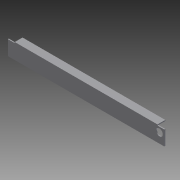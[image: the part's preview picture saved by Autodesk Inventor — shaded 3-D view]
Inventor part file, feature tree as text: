
AUTODESK INVENTOR PART (.ipt)
format: ipt  version: 2012 (Build 160160000, 160)  size: 93,696 bytes
history: native  units: in
note: dims shown in document units (in); Inventor stores cm internally (conversion verified against a paired STEP export)
features: extrude x3, sketch x3
ambient origin geometry x8: Origin, YZ Plane, XZ Plane, XY Plane, X Axis, Y Axis, Z Axis, Center Point
bodies: Solid1 (feature_tree)
feature tree (6):
  extrude  "Extrusion1"  Depth=1.0in
  extrude  "Extrusion2"  Depth=0.125in
  extrude  "Extrusion3"  Depth=20.0in TaperAngle=0.0deg
  sketch  "Sketch1"  dims[d0=2.0in d1=1.0in]
  sketch  "Sketch2"  dims[d2=0.125in d3=0.125in]
  sketch  "Sketch3"  dims[d4=20.0in d5=0.0in d11=20.0in d12=0.0in d13=0.75in d14=0.625in d15=0.875in d16=0.875in d17=0.125in d18=0.0in d19=0.875in]
